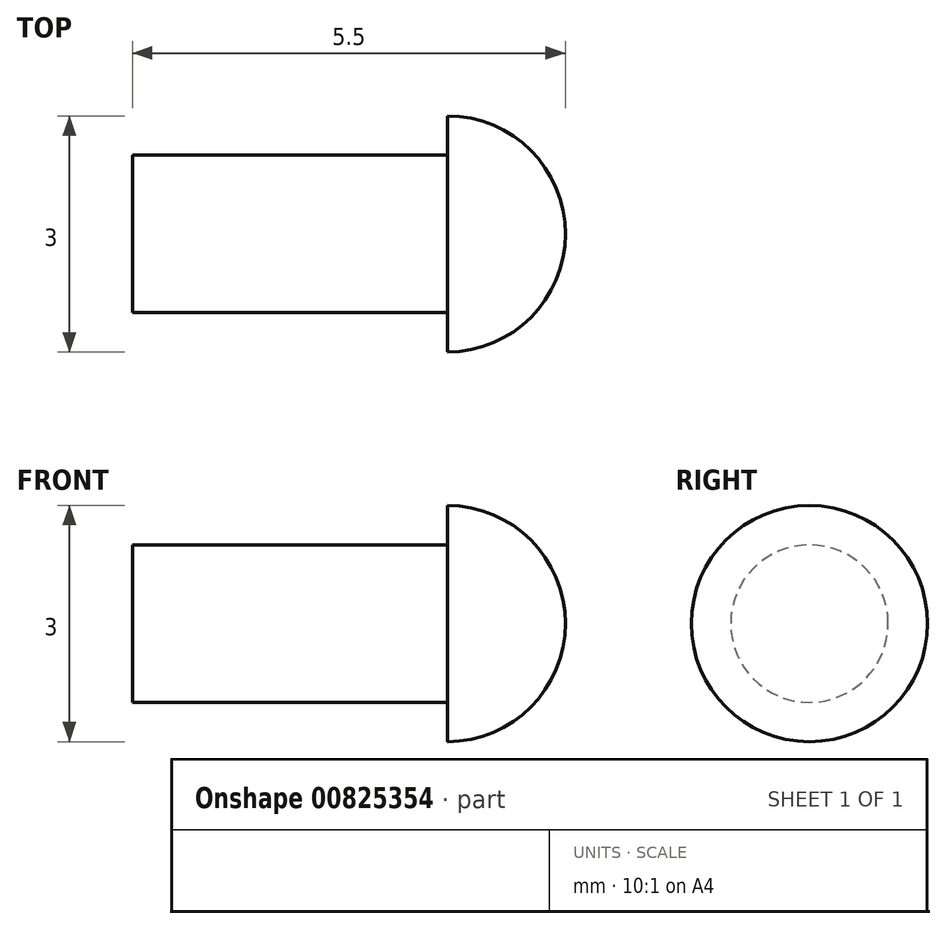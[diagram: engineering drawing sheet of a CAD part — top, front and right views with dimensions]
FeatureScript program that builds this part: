
annotation { "Feature Type Name" : "Feature", "Feature Type Description" : "" }
export const myFeature = defineFeature(function(context is Context, id is Id, definition is map)
    precondition{}
    {
        {
            var Q0;
            Q0=qCreatedBy(makeId("Right.planeOp"),FACE);
            var sketch = newSketch(context, id + "F0", { "sketchPlane" : qUnion([Q0])});
            skCircle(sketch, "E0", {"center": v(0, 0) * mm, "radius": 1 * mm});
            skSolve(sketch);
        }
        {
            var Q0;
            Q0=makeQuery(id+"F0.imprint","IMPRINT",FACE,{"disambiguationData":[TD([[makeQuery(id+"F0.imprint","IMPRINT",EDGE,{"derivedFrom":sQuery(id+"F0.wireOp",EDGE,"E0")}),1.0]])]});
            extrude(context, id + "F1", {"entities" : qUnion([Q0]), "endBound" : BoundingType.SYMMETRIC, "depth" : 4 * mm, "offsetDistance" : 25 * mm});
        }
        {
            var Q0;
            Q0=makeQuery(id+"F1.opExtrude","CAP_FACE",FACE,{"disambiguationData":[OSD([sQuery(id+"F0.wireOp",EDGE,"E0")])],"isStart":false});
            var sketch = newSketch(context, id + "F2", { "sketchPlane" : qUnion([Q0])});
            skArc(sketch, "E1", {"start": v(0, 1.5) * mm, "mid": v(-1.5, 0) * mm, "end": v(0, -1.5) * mm});
            skLineSegment(sketch, "E2", {"start": v(0, 1.5) * mm, "end": v(0, -1.5) * mm});
            skSolve(sketch);
        }
        {
            var Q0;
            Q0 = qSketchRegion(id + "F2", true);
            var Q1;
            Q1=sQuery(id+"F2.wireOp",EDGE,"E2");
            revolve(context, id + "F3", {"operationType" : NewBodyOperationType.ADD, "surfaceOperationType" : NewSurfaceOperationType.NEW, "entities" : qUnion([Q0]), "axis" : qUnion([Q1]), "revolveType" : RevolveType.ONE_DIRECTION, "oppositeDirection" : true, "angle" : 180 * degree});
        }
    });
